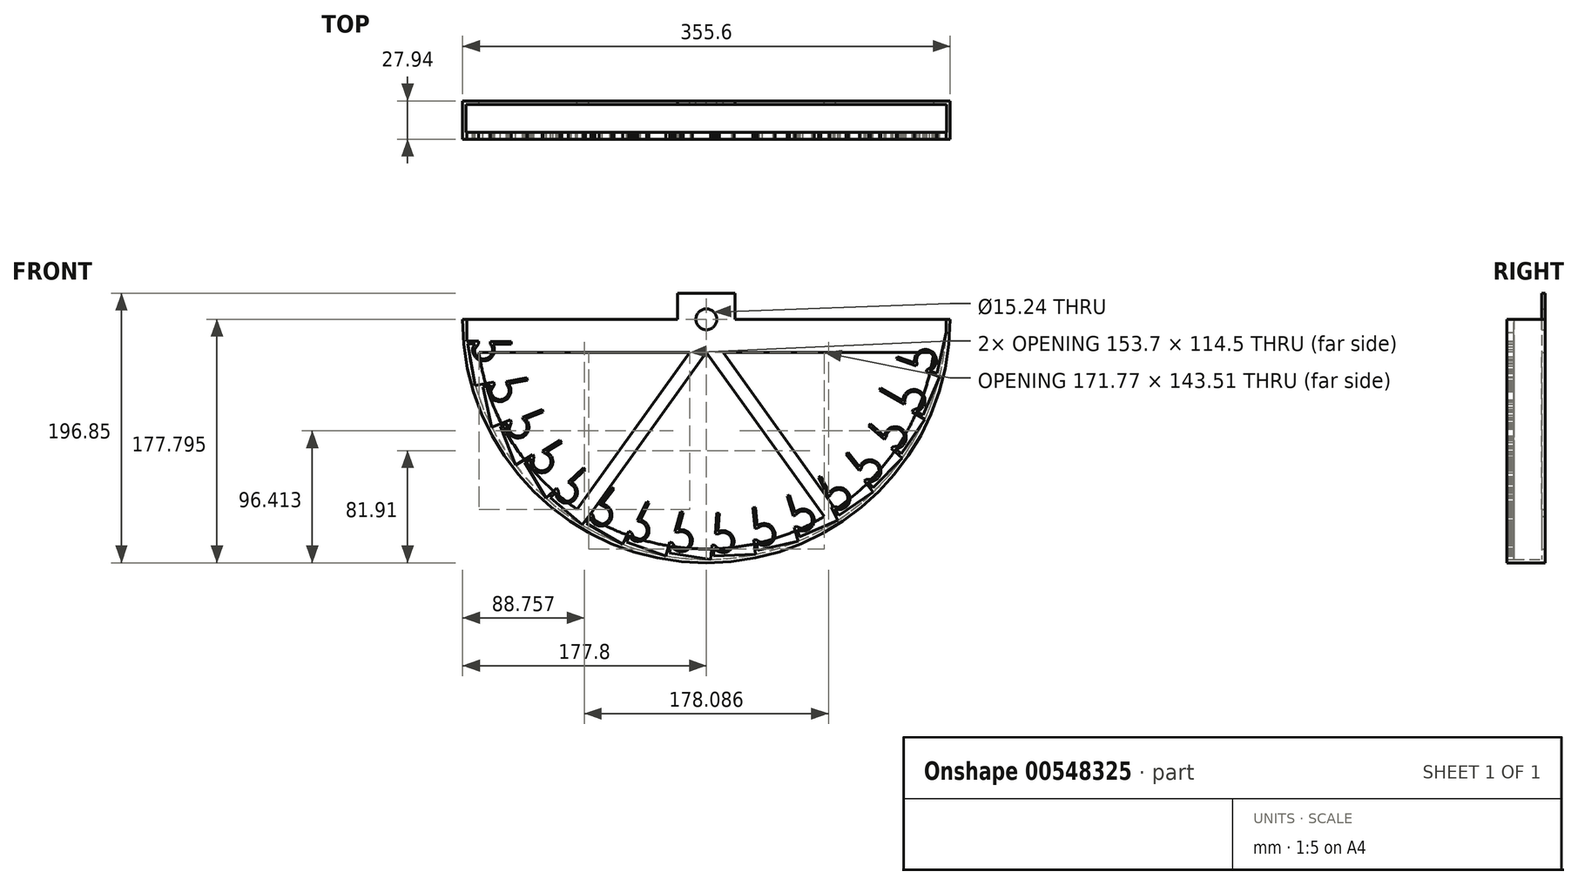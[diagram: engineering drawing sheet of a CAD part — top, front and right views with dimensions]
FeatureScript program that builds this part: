
annotation { "Feature Type Name" : "Feature", "Feature Type Description" : "" }
export const myFeature = defineFeature(function(context is Context, id is Id, definition is map)
    precondition{}
    {
        {
            var Q0;
            Q0=qCreatedBy(makeId("Front.planeOp"),FACE);
            var sketch = newSketch(context, id + "F0", { "sketchPlane" : qUnion([Q0])});
            skArc(sketch, "E0", {"start": v(-177.8, 177.3) * mm, "mid": v(0, -0.5) * mm, "end": v(177.8, 177.3) * mm});
            skLineSegment(sketch, "E1", {"start": v(0, 177.3) * mm, "end": v(177.8, 177.3) * mm});
            skLineSegment(sketch, "E2", {"start": v(0, 177.3) * mm, "end": v(-177.8, 177.3) * mm});
            skLineSegment(sketch, "E3.MirrorCS", {"start": v(-142.3, 159.18) * mm, "end": v(-142.3, 161.09) * mm});
            skLineSegment(sketch, "E4.MirrorCS", {"start": v(-166, 159.36) * mm, "end": v(-166.07, 161.26) * mm});
            skArc(sketch, "E5.MirrorCS", {"start": v(-169.1, 155.45) * mm, "mid": v(-160.47, 148.66) * mm, "end": v(-157.47, 159.21) * mm});
            skLineSegment(sketch, "E6.MirrorCS", {"start": v(-170.16, 157.27) * mm, "end": v(-168.5, 159.37) * mm});
            skLineSegment(sketch, "E7.MirrorCS", {"start": v(-174.1, 159.4) * mm, "end": v(-168.5, 159.37) * mm});
            skLineSegment(sketch, "E8.MirrorCS", {"start": v(-155.76, 159.25) * mm, "end": v(-142.3, 159.18) * mm});
            skLineSegment(sketch, "E9.MirrorCS", {"start": v(-142.3, 161.09) * mm, "end": v(-157.54, 161.16) * mm});
            skArc(sketch, "E10.MirrorCS", {"start": v(-170.16, 157.27) * mm, "mid": v(-161.42, 147.02) * mm, "end": v(-155.76, 159.25) * mm});
            skLineSegment(sketch, "E11.MirrorCS", {"start": v(-166.07, 161.26) * mm, "end": v(-174.53, 161.3) * mm});
            skLineSegment(sketch, "E12.MirrorCS", {"start": v(-166, 159.36) * mm, "end": v(-169.1, 155.45) * mm});
            skLineSegment(sketch, "E13", {"start": v(-174.1, 159.4) * mm, "end": v(-168.5, 129.1) * mm});
            skLineSegment(sketch, "E14", {"start": v(-162.95, 128.2) * mm, "end": v(-156.6, 98.59) * mm});
            skLineSegment(sketch, "E15.MirrorCS", {"start": v(-130.5, 132.86) * mm, "end": v(-130.84, 134.73) * mm});
            skLineSegment(sketch, "E16.MirrorCS", {"start": v(-154.75, 129.7) * mm, "end": v(-155.1, 131.58) * mm});
            skArc(sketch, "E17.MirrorCS", {"start": v(-157.1, 125.2) * mm, "mid": v(-148.27, 119.02) * mm, "end": v(-145.36, 129.4) * mm});
            skLineSegment(sketch, "E18.MirrorCS", {"start": v(-157.54, 129.03) * mm, "end": v(-157.45, 129.2) * mm});
            skLineSegment(sketch, "E19.MirrorCS", {"start": v(-162.95, 128.2) * mm, "end": v(-157.45, 129.2) * mm});
            skLineSegment(sketch, "E20.MirrorCS", {"start": v(-144.3, 130.3) * mm, "end": v(-130.5, 132.86) * mm});
            skLineSegment(sketch, "E21.MirrorCS", {"start": v(-130.84, 134.73) * mm, "end": v(-145.83, 131.96) * mm});
            skArc(sketch, "E22.MirrorCS", {"start": v(-157.54, 129.03) * mm, "mid": v(-149.72, 117.28) * mm, "end": v(-144.3, 130.3) * mm});
            skLineSegment(sketch, "E23.MirrorCS", {"start": v(-145.83, 131.96) * mm, "end": v(-145.36, 129.4) * mm});
            skLineSegment(sketch, "E24.MirrorCS", {"start": v(-155.1, 131.58) * mm, "end": v(-168.5, 129.1) * mm});
            skLineSegment(sketch, "E25.MirrorCS", {"start": v(-154.75, 129.7) * mm, "end": v(-157.1, 125.2) * mm});
            skLineSegment(sketch, "E26.MirrorCS", {"start": v(-119.21, 109.69) * mm, "end": v(-119.9, 111.46) * mm});
            skLineSegment(sketch, "E27.MirrorCS", {"start": v(-142.33, 102.07) * mm, "end": v(-143.02, 103.85) * mm});
            skArc(sketch, "E28.MirrorCS", {"start": v(-143.8, 97.2) * mm, "mid": v(-133.82, 93.07) * mm, "end": v(-133.3, 103.86) * mm});
            skLineSegment(sketch, "E29.MirrorCS", {"start": v(-145.22, 100.13) * mm, "end": v(-144.94, 101.06) * mm});
            skLineSegment(sketch, "E30.MirrorCS", {"start": v(-150.15, 99.04) * mm, "end": v(-144.94, 101.06) * mm});
            skLineSegment(sketch, "E31.MirrorCS", {"start": v(-132.1, 104.69) * mm, "end": v(-119.21, 109.69) * mm});
            skLineSegment(sketch, "E32.MirrorCS", {"start": v(-119.9, 111.46) * mm, "end": v(-134.1, 105.95) * mm});
            skArc(sketch, "E33.MirrorCS", {"start": v(-145.22, 100.13) * mm, "mid": v(-134.73, 91.1) * mm, "end": v(-132.1, 104.69) * mm});
            skLineSegment(sketch, "E34.MirrorCS", {"start": v(-134.1, 105.95) * mm, "end": v(-133.3, 103.86) * mm});
            skLineSegment(sketch, "E35.MirrorCS", {"start": v(-143.02, 103.85) * mm, "end": v(-156.6, 98.59) * mm});
            skLineSegment(sketch, "E36.MirrorCS", {"start": v(-142.33, 102.07) * mm, "end": v(-143.8, 97.2) * mm});
            skLineSegment(sketch, "E37", {"start": v(-174.53, 177.3) * mm, "end": v(-174.53, 161.3) * mm});
            skLineSegment(sketch, "E38", {"start": v(-150.15, 99.04) * mm, "end": v(-139.2, 70.82) * mm});
            skLineSegment(sketch, "E39", {"start": v(-174.53, 161.3) * mm, "end": v(0, 177.3) * mm, "construction": true});
            skLineSegment(sketch, "E40", {"start": v(-168.5, 129.1) * mm, "end": v(0, 177.3) * mm, "construction": true});
            skLineSegment(sketch, "E41", {"start": v(-156.6, 98.59) * mm, "end": v(0, 177.3) * mm, "construction": true});
            skLineSegment(sketch, "E42", {"start": v(-139.2, 70.82) * mm, "end": v(0, 177.3) * mm, "construction": true});
            skLineSegment(sketch, "E43", {"start": v(-174.1, 159.4) * mm, "end": v(-174.45, 161.3) * mm, "construction": true});
            skLineSegment(sketch, "E44", {"start": v(-162.95, 128.2) * mm, "end": v(-163.35, 130.05) * mm, "construction": true});
            skLineSegment(sketch, "E45", {"start": v(-150.15, 99.04) * mm, "end": v(-150.84, 100.82) * mm, "construction": true});
            skLineSegment(sketch, "E46", {"start": v(0, 177.3) * mm, "end": v(-116.96, 46.77) * mm, "construction": true});
            skLineSegment(sketch, "E47", {"start": v(-132.44, 72.79) * mm, "end": v(-116.96, 46.77) * mm});
            skLineSegment(sketch, "E48.MirrorCS", {"start": v(-88.28, 67.45) * mm, "end": v(-89.57, 68.85) * mm});
            skLineSegment(sketch, "E49.MirrorCS", {"start": v(-107.92, 52.51) * mm, "end": v(-109.2, 53.91) * mm});
            skArc(sketch, "E50.MirrorCS", {"start": v(-107.5, 47.45) * mm, "mid": v(-97.11, 46.67) * mm, "end": v(-98.9, 56.94) * mm});
            skLineSegment(sketch, "E51.MirrorCS", {"start": v(-109.3, 47.8) * mm, "end": v(-109.55, 51) * mm});
            skLineSegment(sketch, "E52.MirrorCS", {"start": v(-113.66, 47.22) * mm, "end": v(-109.55, 51) * mm});
            skLineSegment(sketch, "E53.MirrorCS", {"start": v(-98.31, 58.2) * mm, "end": v(-88.28, 67.45) * mm});
            skLineSegment(sketch, "E54.MirrorCS", {"start": v(-89.57, 68.85) * mm, "end": v(-100.78, 58.52) * mm});
            skLineSegment(sketch, "E55.MirrorCS", {"start": v(-109.2, 53.91) * mm, "end": v(-116.96, 46.77) * mm});
            skLineSegment(sketch, "E56.MirrorCS", {"start": v(-107.92, 52.51) * mm, "end": v(-107.5, 47.45) * mm});
            skLineSegment(sketch, "E57", {"start": v(-109.55, 51) * mm, "end": v(-98.31, 58.2) * mm, "construction": true});
            skLineSegment(sketch, "E58", {"start": v(-113.66, 47.22) * mm, "end": v(-90.63, 27.29) * mm});
            skLineSegment(sketch, "E59", {"start": v(-90.63, 27.29) * mm, "end": v(0, 177.3) * mm, "construction": true});
            skLineSegment(sketch, "E60.MirrorCS", {"start": v(-67.5, 53.57) * mm, "end": v(-69.03, 54.7) * mm});
            skLineSegment(sketch, "E61.MirrorCS", {"start": v(-82.81, 34.6) * mm, "end": v(-84.34, 35.75) * mm});
            skArc(sketch, "E62.MirrorCS", {"start": v(-81.47, 29.71) * mm, "mid": v(-70.86, 31.55) * mm, "end": v(-76.08, 40.96) * mm});
            skLineSegment(sketch, "E63.MirrorCS", {"start": v(-87.47, 28.34) * mm, "end": v(-84.14, 32.82) * mm});
            skLineSegment(sketch, "E64.MirrorCS", {"start": v(-75.85, 42.34) * mm, "end": v(-67.5, 53.57) * mm});
            skLineSegment(sketch, "E65.MirrorCS", {"start": v(-69.03, 54.7) * mm, "end": v(-78.12, 42.48) * mm});
            skArc(sketch, "E66.MirrorCS", {"start": v(-83.27, 29.68) * mm, "mid": v(-69.91, 30.35) * mm, "end": v(-75.85, 42.34) * mm});
            skLineSegment(sketch, "E67.MirrorCS", {"start": v(-78.12, 42.48) * mm, "end": v(-76.08, 40.96) * mm});
            skLineSegment(sketch, "E68.MirrorCS", {"start": v(-84.34, 35.75) * mm, "end": v(-90.63, 27.29) * mm});
            skLineSegment(sketch, "E69.MirrorCS", {"start": v(-82.81, 34.6) * mm, "end": v(-81.47, 29.71) * mm});
            skArc(sketch, "E70.trimOffspring", {"start": v(-109.3, 47.8) * mm, "mid": v(-96.5, 45.3) * mm, "end": v(-98.31, 58.2) * mm});
            skLineSegment(sketch, "E71", {"start": v(-82.81, 34.6) * mm, "end": v(-76.08, 40.96) * mm, "construction": true});
            skLineSegment(sketch, "E72", {"start": v(-84.14, 32.82) * mm, "end": v(-83.27, 29.68) * mm});
            skLineSegment(sketch, "E73.MirrorCS", {"start": v(-41.93, 43.33) * mm, "end": v(-43.64, 44.16) * mm});
            skLineSegment(sketch, "E74.MirrorCS", {"start": v(-54.81, 21.7) * mm, "end": v(-56.52, 22.52) * mm});
            skArc(sketch, "E75.MirrorCS", {"start": v(-52.58, 17.13) * mm, "mid": v(-43.55, 21.13) * mm, "end": v(-48.59, 29.62) * mm});
            skLineSegment(sketch, "E76.MirrorCS", {"start": v(-54.18, 16.42) * mm, "end": v(-55.78, 19.7) * mm});
            skLineSegment(sketch, "E77.MirrorCS", {"start": v(-58.23, 14.66) * mm, "end": v(-55.78, 19.7) * mm});
            skLineSegment(sketch, "E78.MirrorCS", {"start": v(-47.96, 30.92) * mm, "end": v(-41.93, 43.33) * mm});
            skLineSegment(sketch, "E79.MirrorCS", {"start": v(-43.64, 44.16) * mm, "end": v(-50.3, 30.46) * mm});
            skArc(sketch, "E80.MirrorCS", {"start": v(-54.18, 16.42) * mm, "mid": v(-42.49, 19.98) * mm, "end": v(-47.96, 30.92) * mm});
            skLineSegment(sketch, "E81.MirrorCS", {"start": v(-50.3, 30.46) * mm, "end": v(-48.59, 29.62) * mm});
            skLineSegment(sketch, "E82.MirrorCS", {"start": v(-56.52, 22.52) * mm, "end": v(-61.13, 13.04) * mm});
            skLineSegment(sketch, "E83.MirrorCS", {"start": v(-54.81, 21.7) * mm, "end": v(-52.58, 17.13) * mm});
            skLineSegment(sketch, "E84", {"start": v(0, 177.3) * mm, "end": v(-29.92, 2.03) * mm, "construction": true});
            skLineSegment(sketch, "E85", {"start": v(-58.23, 14.66) * mm, "end": v(-29.5, 4.54) * mm});
            skLineSegment(sketch, "E86", {"start": v(-55.78, 19.7) * mm, "end": v(-48.59, 29.62) * mm, "construction": true});
            skLineSegment(sketch, "E87", {"start": v(0, 177.3) * mm, "end": v(3.21, -0.48) * mm, "construction": true});
            skLineSegment(sketch, "E88", {"start": v(0, 177.3) * mm, "end": v(36.24, 3.23) * mm, "construction": true});
            skLineSegment(sketch, "E89", {"start": v(0, 177.3) * mm, "end": v(68, 13.01) * mm, "construction": true});
            skLineSegment(sketch, "E90", {"start": v(0, 177.3) * mm, "end": v(97.38, 28.54) * mm, "construction": true});
            skLineSegment(sketch, "E91", {"start": v(0, 177.3) * mm, "end": v(123.37, 49.26) * mm, "construction": true});
            skLineSegment(sketch, "E92", {"start": v(0, 177.3) * mm, "end": v(145.04, 74.45) * mm, "construction": true});
            skLineSegment(sketch, "E93.MirrorCS", {"start": v(-16.96, 36.4) * mm, "end": v(-18.8, 36.9) * mm});
            skLineSegment(sketch, "E94.MirrorCS", {"start": v(-24.9, 14.2) * mm, "end": v(-26.74, 14.7) * mm});
            skArc(sketch, "E95.MirrorCS", {"start": v(-21.85, 10.14) * mm, "mid": v(-11.66, 15.16) * mm, "end": v(-20.95, 21.7) * mm});
            skLineSegment(sketch, "E96.MirrorCS", {"start": v(-24.1, 10.23) * mm, "end": v(-25.48, 12.06) * mm});
            skLineSegment(sketch, "E97.MirrorCS", {"start": v(-26.94, 6.67) * mm, "end": v(-25.48, 12.06) * mm});
            skLineSegment(sketch, "E98.MirrorCS", {"start": v(-20.5, 23.35) * mm, "end": v(-16.96, 36.4) * mm});
            skLineSegment(sketch, "E99.MirrorCS", {"start": v(-18.8, 36.9) * mm, "end": v(-22.79, 22.2) * mm});
            skArc(sketch, "E100.MirrorCS", {"start": v(-24.1, 10.23) * mm, "mid": v(-10.53, 13.55) * mm, "end": v(-20.5, 23.35) * mm});
            skLineSegment(sketch, "E101.MirrorCS", {"start": v(-22.79, 22.2) * mm, "end": v(-20.95, 21.7) * mm});
            skLineSegment(sketch, "E102.MirrorCS", {"start": v(-26.74, 14.7) * mm, "end": v(-29.5, 4.54) * mm});
            skLineSegment(sketch, "E103.MirrorCS", {"start": v(-24.9, 14.2) * mm, "end": v(-21.85, 10.14) * mm});
            skLineSegment(sketch, "E104", {"start": v(-26.94, 6.67) * mm, "end": v(3.17, 2.06) * mm});
            skLineSegment(sketch, "E105", {"start": v(-25.48, 12.06) * mm, "end": v(-20.95, 21.7) * mm, "construction": true});
            skLineSegment(sketch, "E106", {"start": v(0, 177.3) * mm, "end": v(-61.13, 13.04) * mm, "construction": true});
            skLineSegment(sketch, "E107.MirrorCS", {"start": v(9.56, 35.7) * mm, "end": v(7.66, 35.86) * mm});
            skLineSegment(sketch, "E108.MirrorCS", {"start": v(5.89, 12.42) * mm, "end": v(3.99, 12.57) * mm});
            skArc(sketch, "E109.MirrorCS", {"start": v(9.64, 9) * mm, "mid": v(18.72, 15.82) * mm, "end": v(8.37, 20.51) * mm});
            skLineSegment(sketch, "E110.MirrorCS", {"start": v(7.4, 8.66) * mm, "end": v(5.71, 10.2) * mm});
            skLineSegment(sketch, "E111.MirrorCS", {"start": v(5.28, 4.64) * mm, "end": v(5.71, 10.2) * mm});
            skLineSegment(sketch, "E112.MirrorCS", {"start": v(8.5, 22.22) * mm, "end": v(9.56, 35.7) * mm});
            skLineSegment(sketch, "E113.MirrorCS", {"start": v(7.66, 35.86) * mm, "end": v(6.47, 20.66) * mm});
            skArc(sketch, "E114.MirrorCS", {"start": v(7.4, 8.66) * mm, "mid": v(20.13, 14.45) * mm, "end": v(8.5, 22.22) * mm});
            skLineSegment(sketch, "E115.MirrorCS", {"start": v(6.47, 20.66) * mm, "end": v(8.37, 20.51) * mm});
            skLineSegment(sketch, "E116.MirrorCS", {"start": v(3.99, 12.57) * mm, "end": v(3.17, 2.06) * mm});
            skLineSegment(sketch, "E117.MirrorCS", {"start": v(5.89, 12.42) * mm, "end": v(9.64, 9) * mm});
            skLineSegment(sketch, "E118", {"start": v(5.71, 10.2) * mm, "end": v(8.37, 20.51) * mm, "construction": true});
            skLineSegment(sketch, "E119", {"start": v(5.28, 4.64) * mm, "end": v(35.72, 5.71) * mm});
            skLineSegment(sketch, "E120.MirrorCS", {"start": v(35.74, 39.96) * mm, "end": v(33.85, 39.75) * mm});
            skLineSegment(sketch, "E121.MirrorCS", {"start": v(36.47, 16.4) * mm, "end": v(34.57, 16.2) * mm});
            skArc(sketch, "E122.MirrorCS", {"start": v(40.79, 13.73) * mm, "mid": v(48.44, 22.12) * mm, "end": v(37.4, 24.81) * mm});
            skLineSegment(sketch, "E123.MirrorCS", {"start": v(38.66, 12.99) * mm, "end": v(36.7, 14.19) * mm});
            skLineSegment(sketch, "E124.MirrorCS", {"start": v(37.32, 8.63) * mm, "end": v(36.7, 14.19) * mm});
            skLineSegment(sketch, "E125.MirrorCS", {"start": v(37.22, 26.51) * mm, "end": v(35.74, 39.96) * mm});
            skLineSegment(sketch, "E126.MirrorCS", {"start": v(33.85, 39.75) * mm, "end": v(35.5, 24.6) * mm});
            skArc(sketch, "E127.MirrorCS", {"start": v(38.66, 12.99) * mm, "mid": v(50.08, 21.04) * mm, "end": v(37.22, 26.51) * mm});
            skLineSegment(sketch, "E128.MirrorCS", {"start": v(35.5, 24.6) * mm, "end": v(37.4, 24.81) * mm});
            skLineSegment(sketch, "E129.MirrorCS", {"start": v(34.57, 16.2) * mm, "end": v(35.72, 5.71) * mm});
            skLineSegment(sketch, "E130.MirrorCS", {"start": v(36.47, 16.4) * mm, "end": v(40.79, 13.73) * mm});
            skLineSegment(sketch, "E131", {"start": v(36.7, 14.19) * mm, "end": v(37.4, 24.81) * mm, "construction": true});
            skLineSegment(sketch, "E132", {"start": v(37.32, 8.63) * mm, "end": v(67.03, 15.36) * mm});
            skLineSegment(sketch, "E133.MirrorCS", {"start": v(60.67, 49.01) * mm, "end": v(58.85, 48.45) * mm});
            skLineSegment(sketch, "E134.MirrorCS", {"start": v(65.77, 26) * mm, "end": v(63.95, 25.44) * mm});
            skArc(sketch, "E135.MirrorCS", {"start": v(70.51, 24.18) * mm, "mid": v(76.47, 33.85) * mm, "end": v(65.13, 34.44) * mm});
            skLineSegment(sketch, "E136.MirrorCS", {"start": v(68.56, 23.05) * mm, "end": v(66.42, 23.87) * mm});
            skLineSegment(sketch, "E137.MirrorCS", {"start": v(68.05, 18.53) * mm, "end": v(66.42, 23.87) * mm});
            skLineSegment(sketch, "E138.MirrorCS", {"start": v(64.63, 36.07) * mm, "end": v(60.67, 49.01) * mm});
            skLineSegment(sketch, "E139.MirrorCS", {"start": v(58.85, 48.45) * mm, "end": v(63.3, 33.88) * mm});
            skArc(sketch, "E140.MirrorCS", {"start": v(68.56, 23.05) * mm, "mid": v(78.29, 33.1) * mm, "end": v(64.63, 36.07) * mm});
            skLineSegment(sketch, "E141.MirrorCS", {"start": v(63.3, 33.88) * mm, "end": v(65.13, 34.44) * mm});
            skLineSegment(sketch, "E142.MirrorCS", {"start": v(63.95, 25.44) * mm, "end": v(67.03, 15.36) * mm});
            skLineSegment(sketch, "E143.MirrorCS", {"start": v(65.77, 26) * mm, "end": v(70.51, 24.18) * mm});
            skLineSegment(sketch, "E144", {"start": v(66.42, 23.87) * mm, "end": v(65.13, 34.44) * mm, "construction": true});
            skLineSegment(sketch, "E145", {"start": v(68.05, 18.53) * mm, "end": v(96, 30.66) * mm});
            skLineSegment(sketch, "E146.MirrorCS", {"start": v(83.49, 62.54) * mm, "end": v(81.8, 61.66) * mm});
            skLineSegment(sketch, "E147.MirrorCS", {"start": v(92.78, 40.88) * mm, "end": v(91.1, 40) * mm});
            skArc(sketch, "E148.MirrorCS", {"start": v(97.78, 39.97) * mm, "mid": v(101.83, 50.59) * mm, "end": v(90.57, 49.05) * mm});
            skLineSegment(sketch, "E149.MirrorCS", {"start": v(96.06, 38.5) * mm, "end": v(93.81, 38.91) * mm});
            skLineSegment(sketch, "E150.MirrorCS", {"start": v(96.41, 33.96) * mm, "end": v(93.81, 38.91) * mm});
            skLineSegment(sketch, "E151.MirrorCS", {"start": v(89.78, 50.57) * mm, "end": v(83.49, 62.54) * mm});
            skLineSegment(sketch, "E152.MirrorCS", {"start": v(81.8, 61.66) * mm, "end": v(88.89, 48.17) * mm});
            skArc(sketch, "E153.MirrorCS", {"start": v(96.06, 38.5) * mm, "mid": v(103.75, 50.18) * mm, "end": v(89.78, 50.57) * mm});
            skLineSegment(sketch, "E154.MirrorCS", {"start": v(88.89, 48.17) * mm, "end": v(90.57, 49.05) * mm});
            skLineSegment(sketch, "E155.MirrorCS", {"start": v(91.1, 40) * mm, "end": v(96, 30.66) * mm});
            skLineSegment(sketch, "E156.MirrorCS", {"start": v(92.78, 40.88) * mm, "end": v(97.78, 39.97) * mm});
            skLineSegment(sketch, "E157", {"start": v(93.81, 38.91) * mm, "end": v(90.57, 49.05) * mm, "construction": true});
            skLineSegment(sketch, "E158", {"start": v(96.41, 33.96) * mm, "end": v(121.6, 51.09) * mm});
            skLineSegment(sketch, "E159.MirrorCS", {"start": v(103.38, 80.08) * mm, "end": v(101.9, 78.9) * mm});
            skLineSegment(sketch, "E160.MirrorCS", {"start": v(116.54, 60.53) * mm, "end": v(115.05, 59.34) * mm});
            skArc(sketch, "E161.MirrorCS", {"start": v(121.62, 60.57) * mm, "mid": v(123.63, 71.75) * mm, "end": v(112.86, 68.15) * mm});
            skLineSegment(sketch, "E162.MirrorCS", {"start": v(120.21, 58.8) * mm, "end": v(117.93, 58.79) * mm});
            skLineSegment(sketch, "E163.MirrorCS", {"start": v(121.4, 54.4) * mm, "end": v(117.93, 58.79) * mm});
            skLineSegment(sketch, "E164.MirrorCS", {"start": v(111.8, 69.49) * mm, "end": v(103.38, 80.08) * mm});
            skLineSegment(sketch, "E165.MirrorCS", {"start": v(101.9, 78.9) * mm, "end": v(111.37, 66.96) * mm});
            skArc(sketch, "E166.MirrorCS", {"start": v(120.21, 58.8) * mm, "mid": v(125.6, 71.7) * mm, "end": v(111.8, 69.49) * mm});
            skLineSegment(sketch, "E167.MirrorCS", {"start": v(111.37, 66.96) * mm, "end": v(112.86, 68.15) * mm});
            skLineSegment(sketch, "E168.MirrorCS", {"start": v(115.05, 59.34) * mm, "end": v(121.6, 51.09) * mm});
            skLineSegment(sketch, "E169.MirrorCS", {"start": v(116.54, 60.53) * mm, "end": v(121.62, 60.57) * mm});
            skLineSegment(sketch, "E170", {"start": v(117.93, 58.79) * mm, "end": v(112.86, 68.15) * mm, "construction": true});
            skLineSegment(sketch, "E171", {"start": v(121.4, 54.4) * mm, "end": v(142.97, 75.92) * mm});
            skLineSegment(sketch, "E172", {"start": v(142.97, 75.92) * mm, "end": v(96.82, 115.8) * mm});
            skLineSegment(sketch, "E173.MirrorCS", {"start": v(119.67, 101.02) * mm, "end": v(118.42, 99.58) * mm});
            skLineSegment(sketch, "E174.MirrorCS", {"start": v(136.24, 84.26) * mm, "end": v(135, 82.82) * mm});
            skArc(sketch, "E175.MirrorCS", {"start": v(141.22, 85.24) * mm, "mid": v(141.11, 96.6) * mm, "end": v(131.2, 91.06) * mm});
            skLineSegment(sketch, "E176.MirrorCS", {"start": v(140.17, 83.25) * mm, "end": v(137.92, 82.8) * mm});
            skLineSegment(sketch, "E177.MirrorCS", {"start": v(142.15, 79.15) * mm, "end": v(137.92, 82.8) * mm});
            skLineSegment(sketch, "E178.MirrorCS", {"start": v(129.9, 92.17) * mm, "end": v(119.67, 101.02) * mm});
            skLineSegment(sketch, "E179.MirrorCS", {"start": v(118.42, 99.58) * mm, "end": v(129.95, 89.61) * mm});
            skArc(sketch, "E180.MirrorCS", {"start": v(140.17, 83.25) * mm, "mid": v(143.05, 96.92) * mm, "end": v(129.9, 92.17) * mm});
            skLineSegment(sketch, "E181.MirrorCS", {"start": v(129.95, 89.61) * mm, "end": v(131.2, 91.06) * mm});
            skLineSegment(sketch, "E182.MirrorCS", {"start": v(135, 82.82) * mm, "end": v(142.97, 75.92) * mm});
            skLineSegment(sketch, "E183.MirrorCS", {"start": v(136.24, 84.26) * mm, "end": v(141.22, 85.24) * mm});
            skLineSegment(sketch, "E184", {"start": v(137.92, 82.8) * mm, "end": v(131.2, 91.06) * mm, "construction": true});
            skLineSegment(sketch, "E185", {"start": v(0, 177.3) * mm, "end": v(161.64, 103.24) * mm, "construction": true});
            skLineSegment(sketch, "E186", {"start": v(0, 177.3) * mm, "end": v(172.6, 134.62) * mm, "construction": true});
            skLineSegment(sketch, "E187", {"start": v(142.15, 79.15) * mm, "end": v(159.33, 104.3) * mm});
            skLineSegment(sketch, "E188.MirrorCS", {"start": v(127.38, 127.17) * mm, "end": v(126.42, 125.52) * mm});
            skLineSegment(sketch, "E189.MirrorCS", {"start": v(151.17, 111.23) * mm, "end": v(150.22, 109.59) * mm});
            skArc(sketch, "E190.MirrorCS", {"start": v(155.89, 113.13) * mm, "mid": v(153.67, 124.27) * mm, "end": v(144.96, 116.98) * mm});
            skLineSegment(sketch, "E191.MirrorCS", {"start": v(155.22, 110.97) * mm, "end": v(153.1, 110.12) * mm});
            skLineSegment(sketch, "E192.MirrorCS", {"start": v(157.93, 107.32) * mm, "end": v(153.1, 110.12) * mm});
            skLineSegment(sketch, "E193.MirrorCS", {"start": v(143.47, 117.84) * mm, "end": v(127.38, 127.17) * mm});
            skLineSegment(sketch, "E194.MirrorCS", {"start": v(126.42, 125.52) * mm, "end": v(144, 115.33) * mm});
            skArc(sketch, "E195.MirrorCS", {"start": v(155.22, 110.97) * mm, "mid": v(155.51, 124.95) * mm, "end": v(143.47, 117.84) * mm});
            skLineSegment(sketch, "E196.MirrorCS", {"start": v(144, 115.33) * mm, "end": v(144.96, 116.98) * mm});
            skLineSegment(sketch, "E197.MirrorCS", {"start": v(150.22, 109.59) * mm, "end": v(159.33, 104.3) * mm});
            skLineSegment(sketch, "E198.MirrorCS", {"start": v(151.17, 111.23) * mm, "end": v(155.89, 113.13) * mm});
            skLineSegment(sketch, "E199", {"start": v(153.1, 110.12) * mm, "end": v(144.96, 116.98) * mm, "construction": true});
            skLineSegment(sketch, "E200", {"start": v(157.93, 107.32) * mm, "end": v(170.14, 135.22) * mm});
            skLineSegment(sketch, "E201.MirrorCS", {"start": v(139.27, 150.07) * mm, "end": v(138.64, 148.27) * mm});
            skLineSegment(sketch, "E202.MirrorCS", {"start": v(160.82, 140.52) * mm, "end": v(160.2, 138.72) * mm});
            skArc(sketch, "E203.MirrorCS", {"start": v(165.1, 143.26) * mm, "mid": v(160.85, 153.8) * mm, "end": v(153.65, 145) * mm});
            skLineSegment(sketch, "E204.MirrorCS", {"start": v(164.85, 141.02) * mm, "end": v(162.92, 139.78) * mm});
            skLineSegment(sketch, "E205.MirrorCS", {"start": v(168.2, 137.93) * mm, "end": v(162.92, 139.78) * mm});
            skLineSegment(sketch, "E206.MirrorCS", {"start": v(152.03, 145.57) * mm, "end": v(139.27, 150.07) * mm});
            skLineSegment(sketch, "E207.MirrorCS", {"start": v(138.64, 148.27) * mm, "end": v(153.02, 143.2) * mm});
            skArc(sketch, "E208.MirrorCS", {"start": v(164.85, 141.02) * mm, "mid": v(162.54, 154.8) * mm, "end": v(152.03, 145.57) * mm});
            skLineSegment(sketch, "E209.MirrorCS", {"start": v(153.02, 143.2) * mm, "end": v(153.65, 145) * mm});
            skLineSegment(sketch, "E210.MirrorCS", {"start": v(160.2, 138.72) * mm, "end": v(170.14, 135.22) * mm});
            skLineSegment(sketch, "E211.MirrorCS", {"start": v(160.82, 140.52) * mm, "end": v(165.1, 143.26) * mm});
            skLineSegment(sketch, "E212", {"start": v(162.92, 139.78) * mm, "end": v(153.65, 145) * mm, "construction": true});
            skLineSegment(sketch, "E213", {"start": v(0, 177.3) * mm, "end": v(177.53, 167.48) * mm, "construction": true});
            skLineSegment(sketch, "E214", {"start": v(168.2, 137.93) * mm, "end": v(175, 167.62) * mm});
            skLineSegment(sketch, "E215", {"start": v(175, 167.62) * mm, "end": v(175, 177.3) * mm});
            skLineSegment(sketch, "E216", {"start": v(-87.47, 28.34) * mm, "end": v(-61.13, 13.04) * mm});
            skLineSegment(sketch, "E217", {"start": v(-20.86, 177.3) * mm, "end": v(-20.86, 196.35) * mm});
            skCircle(sketch, "E218", {"center": v(0, 177.3) * mm, "radius": 7.62 * mm});
            skLineSegment(sketch, "E219.MirrorCS", {"start": v(-105.56, 87.5) * mm, "end": v(-106.56, 89.12) * mm});
            skLineSegment(sketch, "E220.MirrorCS", {"start": v(-125.85, 76.9) * mm, "end": v(-126.85, 78.51) * mm});
            skArc(sketch, "E221.MirrorCS", {"start": v(-126.39, 71.85) * mm, "mid": v(-115.2, 68.69) * mm, "end": v(-118.7, 79.77) * mm});
            skLineSegment(sketch, "E222.MirrorCS", {"start": v(-127.8, 74.76) * mm, "end": v(-127.7, 75.74) * mm});
            skLineSegment(sketch, "E223.MirrorCS", {"start": v(-132.44, 72.79) * mm, "end": v(-127.7, 75.74) * mm});
            skLineSegment(sketch, "E224.MirrorCS", {"start": v(-116.66, 80.58) * mm, "end": v(-105.56, 87.5) * mm});
            skLineSegment(sketch, "E225.MirrorCS", {"start": v(-106.56, 89.12) * mm, "end": v(-119.5, 81.06) * mm});
            skArc(sketch, "E226.MirrorCS", {"start": v(-127.8, 74.76) * mm, "mid": v(-116.24, 66.2) * mm, "end": v(-116.66, 80.58) * mm});
            skLineSegment(sketch, "E227.MirrorCS", {"start": v(-119.5, 81.06) * mm, "end": v(-118.7, 79.77) * mm});
            skLineSegment(sketch, "E228.MirrorCS", {"start": v(-126.85, 78.51) * mm, "end": v(-139.2, 70.82) * mm});
            skLineSegment(sketch, "E229.MirrorCS", {"start": v(-125.85, 76.9) * mm, "end": v(-126.39, 71.85) * mm});
            skLineSegment(sketch, "E230", {"start": v(-98.9, 56.94) * mm, "end": v(-100.78, 58.52) * mm});
            skLineSegment(sketch, "E231", {"start": v(-20.86, 196.35) * mm, "end": v(0, 196.35) * mm});
            skLineSegment(sketch, "E232.MirrorCS", {"start": v(20.86, 196.35) * mm, "end": v(0, 196.35) * mm});
            skLineSegment(sketch, "E233.MirrorCS", {"start": v(20.86, 177.3) * mm, "end": v(20.86, 196.35) * mm});
            skLineSegment(sketch, "E234", {"start": v(-157.47, 159.21) * mm, "end": v(-157.54, 161.16) * mm});
            skSolve(sketch);
        }
        {
            var Q0;
            Q0=qSketchRegion(id+"F0",true);
            extrude(context, id + "F1", {"entities" : qUnion([Q0]), "endBound" : BoundingType.SYMMETRIC, "depth" : 50.8 * mm, "offsetDistance" : 25.4 * mm});
        }
        {
            var Q0;
            Q0=makeQuery(id+"F1.opExtrude","SWEPT_FACE",FACE,{"disambiguationData":[OSD([sQuery(id+"F0.wireOp",EDGE,"E1"),sQuery(id+"F0.wireOp",EDGE,"E2")])]});
            var Q1;
            Q1=makeQuery(id+"F1.opExtrude","SWEPT_FACE",FACE,{"disambiguationData":[OSD([sQuery(id+"F0.wireOp",EDGE,"E217")])]});
            var Q2;
            Q2=makeQuery(id+"F1.opExtrude","SWEPT_FACE",FACE,{"disambiguationData":[OSD([sQuery(id+"F0.wireOp",EDGE,"IKzNIRuS-lt9D-PZX5-G1JW-kbrlMgvdaDML")])]});
            var Q3;
            Q3=makeQuery(id+"F1.opExtrude","SWEPT_FACE",FACE,{"disambiguationData":[OSD([sQuery(id+"F0.wireOp",EDGE,"ju7AKv3p-tV9e-Mq4A-qTnI-Takg7eoSyEy9")])]});
            shell(context, id + "F2", {"entities" : qUnion([Q0, Q1, Q2, Q3]), "thickness" : 2.54 * mm});
        }
        {
            var Q0;
            {var subQ0=sQuery(id+"F0.wireOp",EDGE,"8sBSUSAj-00hb-c3g1-GJDK-NZvKGYPpUrdB");Q0=makeQuery(id+"F0.imprint","IMPRINT",FACE,{"disambiguationData":[TD([[makeQuery(id+"F0.imprint","IMPRINT",EDGE,{"derivedFrom":subQ0}),-1.0]])]});}
            var Q1;
            Q1=makeQuery(id+"F0.imprint","IMPRINT",FACE,{"disambiguationData":[TD([[makeQuery(id+"F0.imprint","IMPRINT",EDGE,{"derivedFrom":sQuery(id+"F0.wireOp",EDGE,"E3.MirrorCS")}),1.0]])]});
            extrude(context, id + "F3", {"entities" : qUnion([Q0, Q1]), "operationType" : NewBodyOperationType.ADD, "endBound" : BoundingType.SYMMETRIC, "depth" : 5.08 * mm, "offsetDistance" : 25.4 * mm});
        }
        {
            var Q0;
            Q0=makeQuery(id+"F1.opExtrude","CAP_FACE",FACE,{"disambiguationData":[OSD([sQuery(id+"F0.wireOp",EDGE,"E0"),sQuery(id+"F0.wireOp",EDGE,"E1"),sQuery(id+"F0.wireOp",EDGE,"E2"),sQuery(id+"F0.wireOp",EDGE,"4NdIO9du-pqLB-0gZj-tUX9-g2KgcOWVYO3W")])],"isStart":false});
            var sketch = newSketch(context, id + "F4", { "sketchPlane" : qUnion([Q0])});
            skArc(sketch, "E235.0", {"start": v(-166.8, 160.57) * mm, "mid": v(-144.76, 92.76) * mm, "end": v(-96.53, 40.24) * mm});
            skLineSegment(sketch, "E236", {"start": v(0, 153.17) * mm, "end": v(-84.49, 32.5) * mm});
            skLineSegment(sketch, "E237", {"start": v(-12.28, 160.57) * mm, "end": v(-96.53, 40.24) * mm});
            skLineSegment(sketch, "E238", {"start": v(-12.28, 160.57) * mm, "end": v(-166.8, 160.57) * mm});
            skLineSegment(sketch, "E239.MirrorCS", {"start": v(12.2, 160.53) * mm, "end": v(166.8, 160.57) * mm});
            skLineSegment(sketch, "E240.MirrorCS", {"start": v(0, 153.17) * mm, "end": v(84.49, 32.5) * mm});
            skLineSegment(sketch, "E241.MirrorCS", {"start": v(12.2, 160.53) * mm, "end": v(96.53, 40.24) * mm});
            skArc(sketch, "E242.trimOffspring", {"start": v(-84.49, 32.5) * mm, "mid": v(0, 9.66) * mm, "end": v(84.49, 32.5) * mm});
            skArc(sketch, "E243.trimOffspring", {"start": v(96.53, 40.24) * mm, "mid": v(144.76, 92.76) * mm, "end": v(166.8, 160.57) * mm});
            skSolve(sketch);
        }
        {
            var Q0;
            Q0=qSketchRegion(id+"F4",true);
            extrude(context, id + "F5", {"entities" : qUnion([Q0]), "operationType" : NewBodyOperationType.REMOVE, "endBound" : BoundingType.UP_TO_NEXT, "oppositeDirection" : true, "depth" : 25.4 * mm, "offsetDistance" : 25.4 * mm});
        }
        {
            var Q0;
            Q0=makeQuery(id+"F1.opExtrude","CAP_FACE",FACE,{"disambiguationData":[OSD([sQuery(id+"F0.wireOp",EDGE,"E0"),sQuery(id+"F0.wireOp",EDGE,"E1"),sQuery(id+"F0.wireOp",EDGE,"E2"),sQuery(id+"F0.wireOp",EDGE,"E217"),sQuery(id+"F0.wireOp",EDGE,"E218"),sQuery(id+"F0.wireOp",EDGE,"E231"),sQuery(id+"F0.wireOp",EDGE,"E232.MirrorCS"),sQuery(id+"F0.wireOp",EDGE,"E233.MirrorCS")])],"isStart":true});
            var sketch = newSketch(context, id + "F6", { "sketchPlane" : qUnion([Q0])});
            skArc(sketch, "E244.0", {"start": v(165.9, 153.17) * mm, "mid": v(142.12, 88.38) * mm, "end": v(94.25, 38.66) * mm});
            skLineSegment(sketch, "E245", {"start": v(0, 153.17) * mm, "end": v(-85.88, 33.33) * mm});
            skLineSegment(sketch, "E246", {"start": v(-12.2, 153.17) * mm, "end": v(-94.25, 38.66) * mm});
            skLineSegment(sketch, "E247", {"start": v(-12.2, 153.17) * mm, "end": v(-165.9, 153.17) * mm});
            skLineSegment(sketch, "E248.MirrorCS", {"start": v(0, 153.17) * mm, "end": v(85.88, 33.33) * mm});
            skLineSegment(sketch, "E249.MirrorCS", {"start": v(12.2, 153.17) * mm, "end": v(94.25, 38.66) * mm});
            skLineSegment(sketch, "E250.MirrorCS", {"start": v(12.2, 153.17) * mm, "end": v(165.9, 153.17) * mm});
            skArc(sketch, "E251.trimOffspring", {"start": v(-94.25, 38.66) * mm, "mid": v(-142.12, 88.38) * mm, "end": v(-165.9, 153.17) * mm});
            skArc(sketch, "E252.trimOffspring", {"start": v(85.88, 33.33) * mm, "mid": v(0, 9.66) * mm, "end": v(-85.88, 33.33) * mm});
            skSolve(sketch);
        }
        {
            var Q0;
            Q0=qSketchRegion(id+"F6",true);
            extrude(context, id + "F7", {"entities" : qUnion([Q0]), "operationType" : NewBodyOperationType.REMOVE, "endBound" : BoundingType.UP_TO_NEXT, "oppositeDirection" : true, "depth" : 25.4 * mm, "offsetDistance" : 25.4 * mm});
        }
        {
            var Q0;
            Q0=makeQuery(id+"F1.opExtrude","SWEPT_FACE",FACE,{"disambiguationData":[OSD([sQuery(id+"F0.wireOp",EDGE,"E233.MirrorCS")])]});
            var sketch = newSketch(context, id + "F8", { "sketchPlane" : qUnion([Q0])});
            skLineSegment(sketch, "E253", {"start": v(-22.86, 177.3) * mm, "end": v(-22.86, 196.35) * mm});
            skLineSegment(sketch, "E254", {"start": v(-22.86, 196.35) * mm, "end": v(22.86, 196.35) * mm});
            skLineSegment(sketch, "E255", {"start": v(22.86, 196.35) * mm, "end": v(22.86, 177.3) * mm});
            skLineSegment(sketch, "E256", {"start": v(22.86, 177.3) * mm, "end": v(22.86, 161.97) * mm});
            skLineSegment(sketch, "E257", {"start": v(22.86, 161.97) * mm, "end": v(-22.86, 161.97) * mm});
            skLineSegment(sketch, "E258", {"start": v(-22.86, 161.97) * mm, "end": v(-22.86, 177.3) * mm});
            skSolve(sketch);
        }
        {
            var Q0;
            Q0=makeQuery(id+"F8.imprint","IMPRINT",FACE,{"disambiguationData":[TD([[makeQuery(id+"F8.imprint","IMPRINT",EDGE,{"derivedFrom":sQuery(id+"F8.wireOp",EDGE,"E256")}),-1.0]])]});
            var Q1;
            Q1=makeQuery(id+"F8.imprint","IMPRINT",FACE,{"disambiguationData":[TD([[makeQuery(id+"F8.imprint","IMPRINT",EDGE,{"derivedFrom":sQuery(id+"F8.wireOp",EDGE,"E253")}),-1.0]])]});
            extrude(context, id + "F9", {"entities" : qUnion([Q0, Q1]), "operationType" : NewBodyOperationType.REMOVE, "oppositeDirection" : true, "depth" : 52.07 * mm, "offsetDistance" : 25.4 * mm});
        }
        {
            var Q0;
            Q0=makeQuery(id+"F1.opExtrude","CAP_FACE",FACE,{"disambiguationData":[OSD([sQuery(id+"F0.wireOp",EDGE,"E0"),sQuery(id+"F0.wireOp",EDGE,"E1"),sQuery(id+"F0.wireOp",EDGE,"E2"),sQuery(id+"F0.wireOp",EDGE,"E217"),sQuery(id+"F0.wireOp",EDGE,"E218"),sQuery(id+"F0.wireOp",EDGE,"E231"),sQuery(id+"F0.wireOp",EDGE,"E232.MirrorCS"),sQuery(id+"F0.wireOp",EDGE,"E233.MirrorCS")])],"isStart":false});
            var sketch = newSketch(context, id + "F10", { "sketchPlane" : qUnion([Q0])});
            skLineSegment(sketch, "E259.bottom", {"start": v(-246.98, 230.1) * mm, "end": v(251.85, 230.1) * mm});
            skLineSegment(sketch, "E259.top", {"start": v(-246.98, -55.14) * mm, "end": v(251.85, -55.14) * mm});
            skLineSegment(sketch, "E259.left", {"start": v(-246.98, 230.1) * mm, "end": v(-246.98, -55.14) * mm});
            skLineSegment(sketch, "E259.right", {"start": v(251.85, 230.1) * mm, "end": v(251.85, -55.14) * mm});
            skSolve(sketch);
        }
        {
            var Q0;
            Q0 = qSketchRegion(id + "F10", true);
            var Q1;
            {var subQ0=sQuery(id+"F0.wireOp",EDGE,"E223.MirrorCS");var subQ1=sQuery(id+"F0.wireOp",EDGE,"E221.MirrorCS");var subQ2=sQuery(id+"F0.wireOp",EDGE,"E220.MirrorCS");var subQ3=sQuery(id+"F0.wireOp",EDGE,"E55.MirrorCS");var subQ4=sQuery(id+"F0.wireOp",EDGE,"E219.MirrorCS");var subQ5=sQuery(id+"F0.wireOp",EDGE,"E229.MirrorCS");var subQ6=sQuery(id+"F0.wireOp",EDGE,"E228.MirrorCS");var subQ7=sQuery(id+"F0.wireOp",EDGE,"E227.MirrorCS");var subQ8=sQuery(id+"F0.wireOp",EDGE,"E226.MirrorCS");var subQ9=sQuery(id+"F0.wireOp",EDGE,"E225.MirrorCS");var subQ10=sQuery(id+"F0.wireOp",EDGE,"E224.MirrorCS");var subQ11=sQuery(id+"F0.wireOp",EDGE,"E222.MirrorCS");var subQ12=sQuery(id+"F0.wireOp",EDGE,"E47");var subQ13=sQuery(id+"F0.wireOp",EDGE,"E38");var subQ14=sQuery(id+"F0.wireOp",EDGE,"E0");var subQ15=makeQuery(id+"F3.opExtrude","CAP_FACE",FACE,{"disambiguationData":[OSD([subQ14,sQuery(id+"F0.wireOp",EDGE,"E1"),sQuery(id+"F0.wireOp",EDGE,"E2"),sQuery(id+"F0.wireOp",EDGE,"E3.MirrorCS"),sQuery(id+"F0.wireOp",EDGE,"E4.MirrorCS"),sQuery(id+"F0.wireOp",EDGE,"E5.MirrorCS"),sQuery(id+"F0.wireOp",EDGE,"E6.MirrorCS"),sQuery(id+"F0.wireOp",EDGE,"E7.MirrorCS"),sQuery(id+"F0.wireOp",EDGE,"E8.MirrorCS"),sQuery(id+"F0.wireOp",EDGE,"E9.MirrorCS"),sQuery(id+"F0.wireOp",EDGE,"E10.MirrorCS"),sQuery(id+"F0.wireOp",EDGE,"E11.MirrorCS"),sQuery(id+"F0.wireOp",EDGE,"E12.MirrorCS"),sQuery(id+"F0.wireOp",EDGE,"E13"),sQuery(id+"F0.wireOp",EDGE,"E14"),sQuery(id+"F0.wireOp",EDGE,"E15.MirrorCS"),sQuery(id+"F0.wireOp",EDGE,"E16.MirrorCS"),sQuery(id+"F0.wireOp",EDGE,"E17.MirrorCS"),sQuery(id+"F0.wireOp",EDGE,"E18.MirrorCS"),sQuery(id+"F0.wireOp",EDGE,"E19.MirrorCS"),sQuery(id+"F0.wireOp",EDGE,"E20.MirrorCS"),sQuery(id+"F0.wireOp",EDGE,"E21.MirrorCS"),sQuery(id+"F0.wireOp",EDGE,"E22.MirrorCS"),sQuery(id+"F0.wireOp",EDGE,"E23.MirrorCS"),sQuery(id+"F0.wireOp",EDGE,"E24.MirrorCS"),sQuery(id+"F0.wireOp",EDGE,"E25.MirrorCS"),sQuery(id+"F0.wireOp",EDGE,"E26.MirrorCS"),sQuery(id+"F0.wireOp",EDGE,"E27.MirrorCS"),sQuery(id+"F0.wireOp",EDGE,"E28.MirrorCS"),sQuery(id+"F0.wireOp",EDGE,"E29.MirrorCS"),sQuery(id+"F0.wireOp",EDGE,"E30.MirrorCS"),sQuery(id+"F0.wireOp",EDGE,"E31.MirrorCS"),sQuery(id+"F0.wireOp",EDGE,"E32.MirrorCS"),sQuery(id+"F0.wireOp",EDGE,"E33.MirrorCS"),sQuery(id+"F0.wireOp",EDGE,"E34.MirrorCS"),sQuery(id+"F0.wireOp",EDGE,"E35.MirrorCS"),sQuery(id+"F0.wireOp",EDGE,"E36.MirrorCS"),sQuery(id+"F0.wireOp",EDGE,"E37"),subQ13,subQ12,sQuery(id+"F0.wireOp",EDGE,"E48.MirrorCS"),sQuery(id+"F0.wireOp",EDGE,"E49.MirrorCS"),sQuery(id+"F0.wireOp",EDGE,"E50.MirrorCS"),sQuery(id+"F0.wireOp",EDGE,"E51.MirrorCS"),sQuery(id+"F0.wireOp",EDGE,"E52.MirrorCS"),sQuery(id+"F0.wireOp",EDGE,"E53.MirrorCS"),sQuery(id+"F0.wireOp",EDGE,"E54.MirrorCS"),subQ3,sQuery(id+"F0.wireOp",EDGE,"E56.MirrorCS"),sQuery(id+"F0.wireOp",EDGE,"E58"),sQuery(id+"F0.wireOp",EDGE,"E60.MirrorCS"),sQuery(id+"F0.wireOp",EDGE,"E61.MirrorCS"),sQuery(id+"F0.wireOp",EDGE,"E62.MirrorCS"),sQuery(id+"F0.wireOp",EDGE,"E63.MirrorCS"),sQuery(id+"F0.wireOp",EDGE,"E64.MirrorCS"),sQuery(id+"F0.wireOp",EDGE,"E65.MirrorCS"),sQuery(id+"F0.wireOp",EDGE,"E66.MirrorCS"),sQuery(id+"F0.wireOp",EDGE,"E67.MirrorCS"),sQuery(id+"F0.wireOp",EDGE,"E68.MirrorCS"),sQuery(id+"F0.wireOp",EDGE,"E69.MirrorCS"),sQuery(id+"F0.wireOp",EDGE,"E70.trimOffspring"),sQuery(id+"F0.wireOp",EDGE,"E72"),sQuery(id+"F0.wireOp",EDGE,"E73.MirrorCS"),sQuery(id+"F0.wireOp",EDGE,"E74.MirrorCS"),sQuery(id+"F0.wireOp",EDGE,"E75.MirrorCS"),sQuery(id+"F0.wireOp",EDGE,"E76.MirrorCS"),sQuery(id+"F0.wireOp",EDGE,"E77.MirrorCS"),sQuery(id+"F0.wireOp",EDGE,"E78.MirrorCS"),sQuery(id+"F0.wireOp",EDGE,"E79.MirrorCS"),sQuery(id+"F0.wireOp",EDGE,"E80.MirrorCS"),sQuery(id+"F0.wireOp",EDGE,"E81.MirrorCS"),sQuery(id+"F0.wireOp",EDGE,"E82.MirrorCS"),sQuery(id+"F0.wireOp",EDGE,"E83.MirrorCS"),sQuery(id+"F0.wireOp",EDGE,"E85"),sQuery(id+"F0.wireOp",EDGE,"E93.MirrorCS"),sQuery(id+"F0.wireOp",EDGE,"E94.MirrorCS"),sQuery(id+"F0.wireOp",EDGE,"E95.MirrorCS"),sQuery(id+"F0.wireOp",EDGE,"E96.MirrorCS"),sQuery(id+"F0.wireOp",EDGE,"E97.MirrorCS"),sQuery(id+"F0.wireOp",EDGE,"E98.MirrorCS"),sQuery(id+"F0.wireOp",EDGE,"E99.MirrorCS"),sQuery(id+"F0.wireOp",EDGE,"E100.MirrorCS"),sQuery(id+"F0.wireOp",EDGE,"E101.MirrorCS"),sQuery(id+"F0.wireOp",EDGE,"E102.MirrorCS"),sQuery(id+"F0.wireOp",EDGE,"E103.MirrorCS"),sQuery(id+"F0.wireOp",EDGE,"E104"),sQuery(id+"F0.wireOp",EDGE,"E107.MirrorCS"),sQuery(id+"F0.wireOp",EDGE,"E108.MirrorCS"),sQuery(id+"F0.wireOp",EDGE,"E109.MirrorCS"),sQuery(id+"F0.wireOp",EDGE,"E110.MirrorCS"),sQuery(id+"F0.wireOp",EDGE,"E111.MirrorCS"),sQuery(id+"F0.wireOp",EDGE,"E112.MirrorCS"),sQuery(id+"F0.wireOp",EDGE,"E113.MirrorCS"),sQuery(id+"F0.wireOp",EDGE,"E114.MirrorCS"),sQuery(id+"F0.wireOp",EDGE,"E115.MirrorCS"),sQuery(id+"F0.wireOp",EDGE,"E116.MirrorCS"),sQuery(id+"F0.wireOp",EDGE,"E117.MirrorCS"),sQuery(id+"F0.wireOp",EDGE,"E119"),sQuery(id+"F0.wireOp",EDGE,"E120.MirrorCS"),sQuery(id+"F0.wireOp",EDGE,"E121.MirrorCS"),sQuery(id+"F0.wireOp",EDGE,"E122.MirrorCS"),sQuery(id+"F0.wireOp",EDGE,"E123.MirrorCS"),sQuery(id+"F0.wireOp",EDGE,"E124.MirrorCS"),sQuery(id+"F0.wireOp",EDGE,"E125.MirrorCS"),sQuery(id+"F0.wireOp",EDGE,"E126.MirrorCS"),sQuery(id+"F0.wireOp",EDGE,"E127.MirrorCS"),sQuery(id+"F0.wireOp",EDGE,"E128.MirrorCS"),sQuery(id+"F0.wireOp",EDGE,"E129.MirrorCS"),sQuery(id+"F0.wireOp",EDGE,"E130.MirrorCS"),sQuery(id+"F0.wireOp",EDGE,"E132"),sQuery(id+"F0.wireOp",EDGE,"E133.MirrorCS"),sQuery(id+"F0.wireOp",EDGE,"E134.MirrorCS"),sQuery(id+"F0.wireOp",EDGE,"E135.MirrorCS"),sQuery(id+"F0.wireOp",EDGE,"E136.MirrorCS"),sQuery(id+"F0.wireOp",EDGE,"E137.MirrorCS"),sQuery(id+"F0.wireOp",EDGE,"E138.MirrorCS"),sQuery(id+"F0.wireOp",EDGE,"E139.MirrorCS"),sQuery(id+"F0.wireOp",EDGE,"E140.MirrorCS"),sQuery(id+"F0.wireOp",EDGE,"E141.MirrorCS"),sQuery(id+"F0.wireOp",EDGE,"E142.MirrorCS"),sQuery(id+"F0.wireOp",EDGE,"E143.MirrorCS"),sQuery(id+"F0.wireOp",EDGE,"E145"),sQuery(id+"F0.wireOp",EDGE,"E146.MirrorCS"),sQuery(id+"F0.wireOp",EDGE,"E147.MirrorCS"),sQuery(id+"F0.wireOp",EDGE,"E148.MirrorCS"),sQuery(id+"F0.wireOp",EDGE,"E149.MirrorCS"),sQuery(id+"F0.wireOp",EDGE,"E150.MirrorCS"),sQuery(id+"F0.wireOp",EDGE,"E151.MirrorCS"),sQuery(id+"F0.wireOp",EDGE,"E152.MirrorCS"),sQuery(id+"F0.wireOp",EDGE,"E153.MirrorCS"),sQuery(id+"F0.wireOp",EDGE,"E154.MirrorCS"),sQuery(id+"F0.wireOp",EDGE,"E155.MirrorCS"),sQuery(id+"F0.wireOp",EDGE,"E156.MirrorCS"),sQuery(id+"F0.wireOp",EDGE,"E158"),sQuery(id+"F0.wireOp",EDGE,"E159.MirrorCS"),sQuery(id+"F0.wireOp",EDGE,"E160.MirrorCS"),sQuery(id+"F0.wireOp",EDGE,"E161.MirrorCS"),sQuery(id+"F0.wireOp",EDGE,"E162.MirrorCS"),sQuery(id+"F0.wireOp",EDGE,"E163.MirrorCS"),sQuery(id+"F0.wireOp",EDGE,"E164.MirrorCS"),sQuery(id+"F0.wireOp",EDGE,"E165.MirrorCS"),sQuery(id+"F0.wireOp",EDGE,"E166.MirrorCS"),sQuery(id+"F0.wireOp",EDGE,"E167.MirrorCS"),sQuery(id+"F0.wireOp",EDGE,"E168.MirrorCS"),sQuery(id+"F0.wireOp",EDGE,"E169.MirrorCS"),sQuery(id+"F0.wireOp",EDGE,"E171"),sQuery(id+"F0.wireOp",EDGE,"E173.MirrorCS"),sQuery(id+"F0.wireOp",EDGE,"E174.MirrorCS"),sQuery(id+"F0.wireOp",EDGE,"E175.MirrorCS"),sQuery(id+"F0.wireOp",EDGE,"E176.MirrorCS"),sQuery(id+"F0.wireOp",EDGE,"E177.MirrorCS"),sQuery(id+"F0.wireOp",EDGE,"E178.MirrorCS"),sQuery(id+"F0.wireOp",EDGE,"E179.MirrorCS"),sQuery(id+"F0.wireOp",EDGE,"E180.MirrorCS"),sQuery(id+"F0.wireOp",EDGE,"E181.MirrorCS"),sQuery(id+"F0.wireOp",EDGE,"E182.MirrorCS"),sQuery(id+"F0.wireOp",EDGE,"E183.MirrorCS"),sQuery(id+"F0.wireOp",EDGE,"E187"),sQuery(id+"F0.wireOp",EDGE,"E188.MirrorCS"),sQuery(id+"F0.wireOp",EDGE,"E189.MirrorCS"),sQuery(id+"F0.wireOp",EDGE,"E190.MirrorCS"),sQuery(id+"F0.wireOp",EDGE,"E191.MirrorCS"),sQuery(id+"F0.wireOp",EDGE,"E192.MirrorCS"),sQuery(id+"F0.wireOp",EDGE,"E193.MirrorCS"),sQuery(id+"F0.wireOp",EDGE,"E194.MirrorCS"),sQuery(id+"F0.wireOp",EDGE,"E195.MirrorCS"),sQuery(id+"F0.wireOp",EDGE,"E196.MirrorCS"),sQuery(id+"F0.wireOp",EDGE,"E197.MirrorCS"),sQuery(id+"F0.wireOp",EDGE,"E198.MirrorCS"),sQuery(id+"F0.wireOp",EDGE,"E200"),sQuery(id+"F0.wireOp",EDGE,"E201.MirrorCS"),sQuery(id+"F0.wireOp",EDGE,"E202.MirrorCS"),sQuery(id+"F0.wireOp",EDGE,"E203.MirrorCS"),sQuery(id+"F0.wireOp",EDGE,"E204.MirrorCS"),sQuery(id+"F0.wireOp",EDGE,"E205.MirrorCS"),sQuery(id+"F0.wireOp",EDGE,"E206.MirrorCS"),sQuery(id+"F0.wireOp",EDGE,"E207.MirrorCS"),sQuery(id+"F0.wireOp",EDGE,"E208.MirrorCS"),sQuery(id+"F0.wireOp",EDGE,"E209.MirrorCS"),sQuery(id+"F0.wireOp",EDGE,"E210.MirrorCS"),sQuery(id+"F0.wireOp",EDGE,"E211.MirrorCS"),sQuery(id+"F0.wireOp",EDGE,"E214"),sQuery(id+"F0.wireOp",EDGE,"E215"),sQuery(id+"F0.wireOp",EDGE,"E216"),subQ4,subQ2,subQ1,subQ11,subQ0,subQ10,subQ9,subQ8,subQ7,subQ6,subQ5,sQuery(id+"F0.wireOp",EDGE,"E230"),sQuery(id+"F0.wireOp",EDGE,"E234")])],"isStart":false});Q1=makeQuery(id+"F3.boolean.opBoolean","SPLIT",FACE,{"disambiguationData":[TD([makeQuery(id+"F3.opExtrude","SWEPT_FACE",FACE,{"disambiguationData":[OSD([subQ4])]})])],"derivedFrom":subQ15});}
            extrude(context, id + "F11", {"entities" : qUnion([Q0]), "operationType" : NewBodyOperationType.REMOVE, "endBound" : BoundingType.UP_TO_SURFACE, "oppositeDirection" : true, "depth" : 25.4 * mm, "endBoundEntityFace" : qUnion([Q1]), "offsetDistance" : 25.4 * mm});
        }
    });
